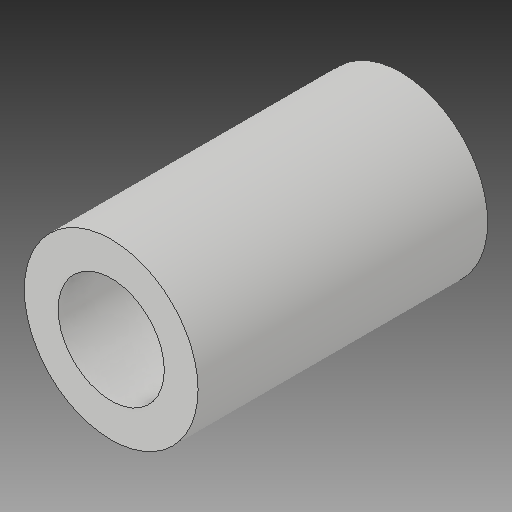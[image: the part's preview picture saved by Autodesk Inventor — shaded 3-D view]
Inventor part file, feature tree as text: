
AUTODESK INVENTOR PART (.ipt)
format: ipt  version: 2017 (Build 210142000, 142)  size: 104,448 bytes
history: native  units: mm
features: other x3, sketch x1
ambient origin geometry x8: Origin, YZ Plane, XZ Plane, XY Plane, X Axis, Y Axis, Z Axis, Center Point
bodies: Solid1 (feature_tree)
feature tree (4):
  other  "Long-Spacer.ipt"
  other  "Solid1::Long-Spacer.ipt"
  other  "TaggingFeature1"
  sketch  "Sketch1"  dims[d0=10.0mm]
